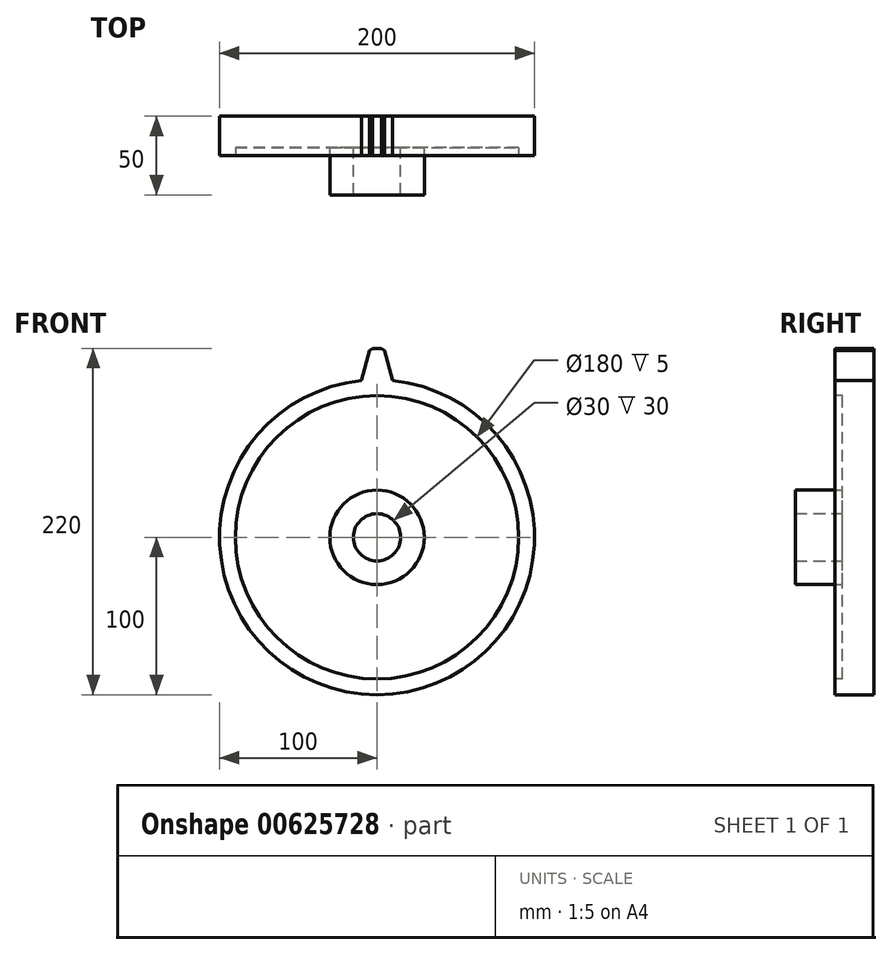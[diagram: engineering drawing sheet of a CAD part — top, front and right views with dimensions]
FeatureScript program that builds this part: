
annotation { "Feature Type Name" : "Feature", "Feature Type Description" : "" }
export const myFeature = defineFeature(function(context is Context, id is Id, definition is map)
    precondition{}
    {
        {
            var Q0;
            Q0=qCreatedBy(makeId("Front.planeOp"),FACE);
            var sketch = newSketch(context, id + "F0", { "sketchPlane" : qUnion([Q0])});
            skCircle(sketch, "E0", {"center": v(0, 0) * mm, "radius": 100 * mm});
            skSolve(sketch);
        }
        {
            var Q0;
            Q0 = qSketchRegion(id + "F0", true);
            extrude(context, id + "F1", {"entities" : qUnion([Q0]), "depth" : 25 * mm, "offsetDistance" : 25 * mm});
        }
        {
            var Q0;
            Q0=makeQuery(id+"F1.opExtrude","CAP_FACE",FACE,{"disambiguationData":[OSD([sQuery(id+"F0.wireOp",EDGE,"E0")])],"isStart":false});
            var sketch = newSketch(context, id + "F2", { "sketchPlane" : qUnion([Q0])});
            skLineSegment(sketch, "E1", {"start": v(-10, 99.5) * mm, "end": v(-4.5, 120) * mm});
            skLineSegment(sketch, "E2", {"start": v(-4.5, 120) * mm, "end": v(4.5, 120) * mm});
            skLineSegment(sketch, "E3", {"start": v(4.5, 120) * mm, "end": v(10, 99.5) * mm});
            skLineSegment(sketch, "E4", {"start": v(10, 99.5) * mm, "end": v(-10, 99.5) * mm});
            skSolve(sketch);
        }
        {
            var Q0;
            Q0 = qSketchRegion(id + "F2", true);
            extrude(context, id + "F3", {"entities" : qUnion([Q0]), "operationType" : NewBodyOperationType.ADD, "oppositeDirection" : true, "depth" : 25 * mm, "offsetDistance" : 25 * mm});
        }
        {
            var Q0;
            Q0=makeQuery(id+"F3.opExtrude","SWEPT_EDGE",EDGE,{"disambiguationData":[OSD([sQuery(id+"F2.wireOp",EDGE,"E2"),sQuery(id+"F2.wireOp",EDGE,"E3")])]});
            var Q1;
            Q1=makeQuery(id+"F3.opExtrude","SWEPT_EDGE",EDGE,{"disambiguationData":[OSD([sQuery(id+"F2.wireOp",EDGE,"E1"),sQuery(id+"F2.wireOp",EDGE,"E2")])]});
            chamfer(context, id + "F4", {"entities" : qUnion([Q0, Q1]), "width" : 2 * mm, "tangentPropagation" : true});
        }
        {
            var Q0;
            Q0=makeQuery(id+"F3.opExtrude","SWEPT_EDGE",EDGE,{"disambiguationData":[OSD([sQuery(id+"F0.wireOp",EDGE,"E0"),sQuery(id+"F2.wireOp",EDGE,"E3"),sQuery(id+"F2.wireOp",EDGE,"E4")])]});
            var Q1;
            Q1=makeQuery(id+"F3.opExtrude","SWEPT_EDGE",EDGE,{"disambiguationData":[OSD([sQuery(id+"F0.wireOp",EDGE,"E0"),sQuery(id+"F2.wireOp",EDGE,"E1"),sQuery(id+"F2.wireOp",EDGE,"E4")])]});
            fillet(context, id + "F5", {"entities" : qUnion([Q0, Q1]), "radius" : 5 * mm, "tangentPropagation" : true, "allowEdgeOverflow" : false});
        }
        {
            var Q0;
            {var subQ0=sQuery(id+"F2.wireOp",EDGE,"E4");var subQ1=sQuery(id+"F2.wireOp",EDGE,"E3");var subQ2=sQuery(id+"F2.wireOp",EDGE,"E2");var subQ3=sQuery(id+"F2.wireOp",EDGE,"E1");Q0=makeQuery(id+"FwmvFuFNIoCn6Q2_1.19.F3.boolean.opBoolean","MERGE",FACE,{"derivedFrom":[makeQuery(id+"FwmvFuFNIoCn6Q2_1.18.F3.boolean.opBoolean","MERGE",FACE,{"derivedFrom":[makeQuery(id+"FwmvFuFNIoCn6Q2_1.17.F3.boolean.opBoolean","MERGE",FACE,{"derivedFrom":[makeQuery(id+"FwmvFuFNIoCn6Q2_1.16.F3.boolean.opBoolean","MERGE",FACE,{"derivedFrom":[makeQuery(id+"FwmvFuFNIoCn6Q2_1.15.F3.boolean.opBoolean","MERGE",FACE,{"derivedFrom":[makeQuery(id+"FwmvFuFNIoCn6Q2_1.14.F3.boolean.opBoolean","MERGE",FACE,{"derivedFrom":[makeQuery(id+"FwmvFuFNIoCn6Q2_1.13.F3.boolean.opBoolean","MERGE",FACE,{"derivedFrom":[makeQuery(id+"FwmvFuFNIoCn6Q2_1.12.F3.boolean.opBoolean","MERGE",FACE,{"derivedFrom":[makeQuery(id+"FwmvFuFNIoCn6Q2_1.11.F3.boolean.opBoolean","MERGE",FACE,{"derivedFrom":[makeQuery(id+"FwmvFuFNIoCn6Q2_1.10.F3.boolean.opBoolean","MERGE",FACE,{"derivedFrom":[makeQuery(id+"FwmvFuFNIoCn6Q2_1.9.F3.boolean.opBoolean","MERGE",FACE,{"derivedFrom":[makeQuery(id+"FwmvFuFNIoCn6Q2_1.8.F3.boolean.opBoolean","MERGE",FACE,{"derivedFrom":[makeQuery(id+"FwmvFuFNIoCn6Q2_1.7.F3.boolean.opBoolean","MERGE",FACE,{"derivedFrom":[makeQuery(id+"FwmvFuFNIoCn6Q2_1.6.F3.boolean.opBoolean","MERGE",FACE,{"derivedFrom":[makeQuery(id+"FwmvFuFNIoCn6Q2_1.5.F3.boolean.opBoolean","MERGE",FACE,{"derivedFrom":[makeQuery(id+"FwmvFuFNIoCn6Q2_1.4.F3.boolean.opBoolean","MERGE",FACE,{"derivedFrom":[makeQuery(id+"FwmvFuFNIoCn6Q2_1.3.F3.boolean.opBoolean","MERGE",FACE,{"derivedFrom":[makeQuery(id+"FwmvFuFNIoCn6Q2_1.2.F3.boolean.opBoolean","MERGE",FACE,{"derivedFrom":[makeQuery(id+"FwmvFuFNIoCn6Q2_1.1.F3.boolean.opBoolean","MERGE",FACE,{"derivedFrom":[makeQuery(id+"F3.boolean.opBoolean","MERGE",FACE,{"derivedFrom":[makeQuery(id+"F1.opExtrude","CAP_FACE",FACE,{"disambiguationData":[OSD([sQuery(id+"F0.wireOp",EDGE,"E0")])],"isStart":false}),makeQuery(id+"F3.opExtrude","CAP_FACE",FACE,{"disambiguationData":[OSD([subQ3,subQ2,subQ1,subQ0])],"isStart":true})]}),makeQuery(id+"FwmvFuFNIoCn6Q2_1.1.F3.opExtrude","CAP_FACE",FACE,{"disambiguationData":[OSD([subQ3,subQ2,subQ1,subQ0])],"isStart":true})]}),makeQuery(id+"FwmvFuFNIoCn6Q2_1.2.F3.opExtrude","CAP_FACE",FACE,{"disambiguationData":[OSD([subQ3,subQ2,subQ1,subQ0])],"isStart":true})]}),makeQuery(id+"FwmvFuFNIoCn6Q2_1.3.F3.opExtrude","CAP_FACE",FACE,{"disambiguationData":[OSD([subQ3,subQ2,subQ1,subQ0])],"isStart":true})]}),makeQuery(id+"FwmvFuFNIoCn6Q2_1.4.F3.opExtrude","CAP_FACE",FACE,{"disambiguationData":[OSD([subQ3,subQ2,subQ1,subQ0])],"isStart":true})]}),makeQuery(id+"FwmvFuFNIoCn6Q2_1.5.F3.opExtrude","CAP_FACE",FACE,{"disambiguationData":[OSD([subQ3,subQ2,subQ1,subQ0])],"isStart":true})]}),makeQuery(id+"FwmvFuFNIoCn6Q2_1.6.F3.opExtrude","CAP_FACE",FACE,{"disambiguationData":[OSD([subQ3,subQ2,subQ1,subQ0])],"isStart":true})]}),makeQuery(id+"FwmvFuFNIoCn6Q2_1.7.F3.opExtrude","CAP_FACE",FACE,{"disambiguationData":[OSD([subQ3,subQ2,subQ1,subQ0])],"isStart":true})]}),makeQuery(id+"FwmvFuFNIoCn6Q2_1.8.F3.opExtrude","CAP_FACE",FACE,{"disambiguationData":[OSD([subQ3,subQ2,subQ1,subQ0])],"isStart":true})]}),makeQuery(id+"FwmvFuFNIoCn6Q2_1.9.F3.opExtrude","CAP_FACE",FACE,{"disambiguationData":[OSD([subQ3,subQ2,subQ1,subQ0])],"isStart":true})]}),makeQuery(id+"FwmvFuFNIoCn6Q2_1.10.F3.opExtrude","CAP_FACE",FACE,{"disambiguationData":[OSD([subQ3,subQ2,subQ1,subQ0])],"isStart":true})]}),makeQuery(id+"FwmvFuFNIoCn6Q2_1.11.F3.opExtrude","CAP_FACE",FACE,{"disambiguationData":[OSD([subQ3,subQ2,subQ1,subQ0])],"isStart":true})]}),makeQuery(id+"FwmvFuFNIoCn6Q2_1.12.F3.opExtrude","CAP_FACE",FACE,{"disambiguationData":[OSD([subQ3,subQ2,subQ1,subQ0])],"isStart":true})]}),makeQuery(id+"FwmvFuFNIoCn6Q2_1.13.F3.opExtrude","CAP_FACE",FACE,{"disambiguationData":[OSD([subQ3,subQ2,subQ1,subQ0])],"isStart":true})]}),makeQuery(id+"FwmvFuFNIoCn6Q2_1.14.F3.opExtrude","CAP_FACE",FACE,{"disambiguationData":[OSD([subQ3,subQ2,subQ1,subQ0])],"isStart":true})]}),makeQuery(id+"FwmvFuFNIoCn6Q2_1.15.F3.opExtrude","CAP_FACE",FACE,{"disambiguationData":[OSD([subQ3,subQ2,subQ1,subQ0])],"isStart":true})]}),makeQuery(id+"FwmvFuFNIoCn6Q2_1.16.F3.opExtrude","CAP_FACE",FACE,{"disambiguationData":[OSD([subQ3,subQ2,subQ1,subQ0])],"isStart":true})]}),makeQuery(id+"FwmvFuFNIoCn6Q2_1.17.F3.opExtrude","CAP_FACE",FACE,{"disambiguationData":[OSD([subQ3,subQ2,subQ1,subQ0])],"isStart":true})]}),makeQuery(id+"FwmvFuFNIoCn6Q2_1.18.F3.opExtrude","CAP_FACE",FACE,{"disambiguationData":[OSD([subQ3,subQ2,subQ1,subQ0])],"isStart":true})]}),makeQuery(id+"FwmvFuFNIoCn6Q2_1.19.F3.opExtrude","CAP_FACE",FACE,{"disambiguationData":[OSD([subQ3,subQ2,subQ1,subQ0])],"isStart":true})]});}
            var sketch = newSketch(context, id + "F6", { "sketchPlane" : qUnion([Q0])});
            skCircle(sketch, "E5", {"center": v(0, 0) * mm, "radius": 90 * mm});
            skSolve(sketch);
        }
        {
            var Q0;
            Q0 = qSketchRegion(id + "F6", true);
            extrude(context, id + "F7", {"entities" : qUnion([Q0]), "operationType" : NewBodyOperationType.REMOVE, "oppositeDirection" : true, "depth" : 5 * mm, "offsetDistance" : 25 * mm});
        }
        {
            var Q0;
            Q0=makeQuery(id+"F7.boolean.opBoolean","COPY",FACE,{"derivedFrom":makeQuery(id+"F7.opExtrude","CAP_FACE",FACE,{"disambiguationData":[OSD([sQuery(id+"F6.wireOp",EDGE,"E5")])],"isStart":false})});
            var sketch = newSketch(context, id + "F8", { "sketchPlane" : qUnion([Q0])});
            skCircle(sketch, "E6", {"center": v(0, 0) * mm, "radius": 15 * mm});
            skCircle(sketch, "E7", {"center": v(0, 0) * mm, "radius": 30 * mm});
            skSolve(sketch);
        }
        {
            var Q0;
            Q0=makeQuery(id+"F8.imprint","IMPRINT",FACE,{"disambiguationData":[TD([[makeQuery(id+"F8.imprint","IMPRINT",EDGE,{"derivedFrom":sQuery(id+"F8.wireOp",EDGE,"E6")}),-1.0]])]});
            extrude(context, id + "F9", {"entities" : qUnion([Q0]), "operationType" : NewBodyOperationType.ADD, "depth" : 30 * mm, "offsetDistance" : 25 * mm});
        }
    });
